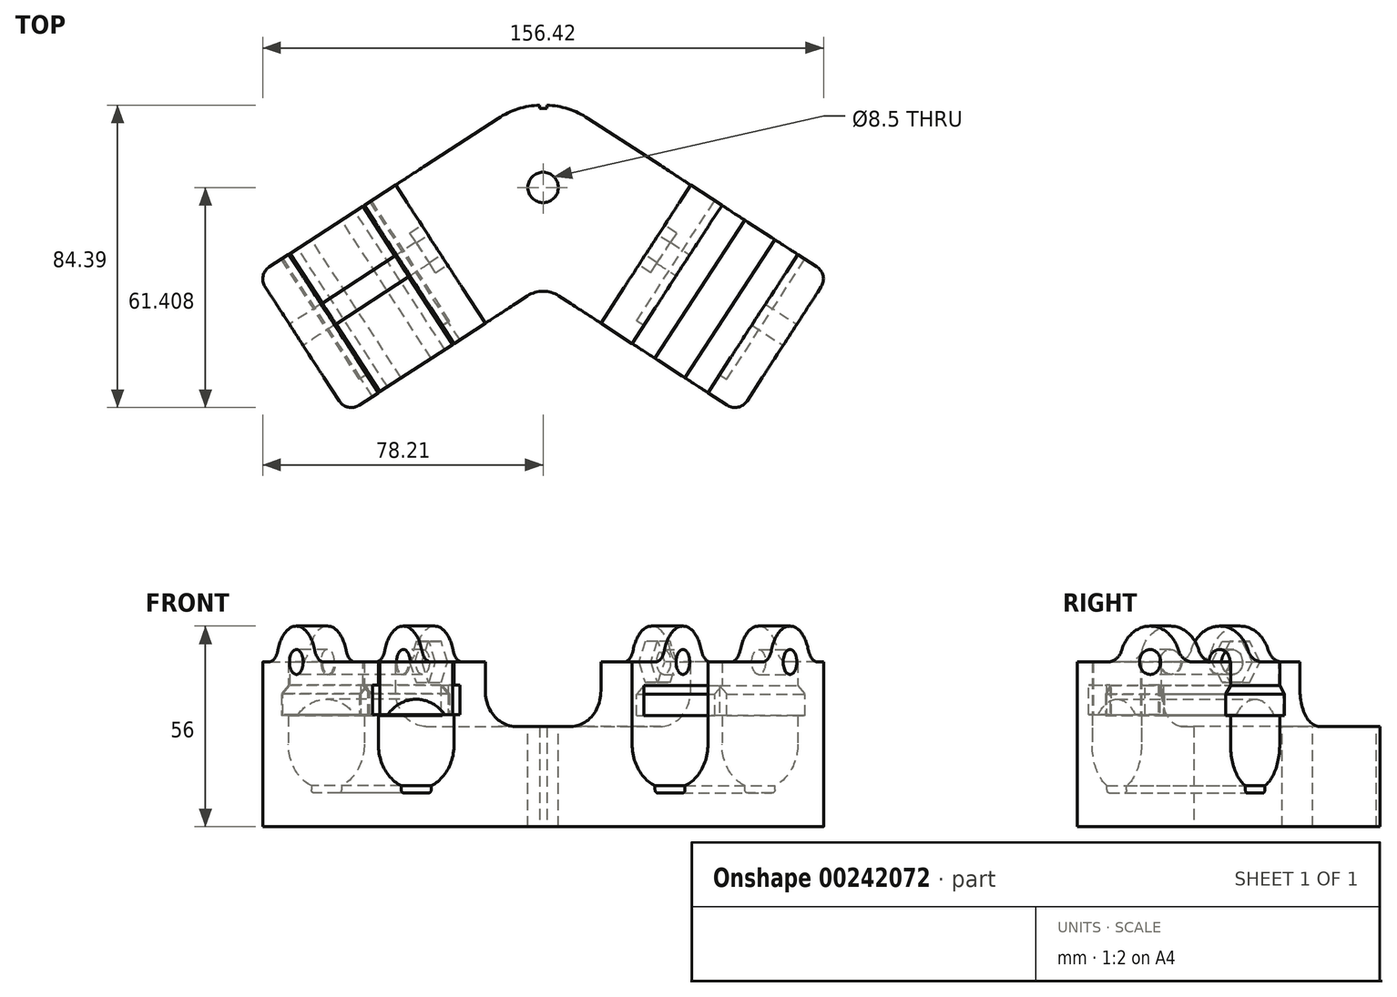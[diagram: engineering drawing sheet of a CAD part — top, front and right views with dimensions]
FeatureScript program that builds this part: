
annotation { "Feature Type Name" : "Feature", "Feature Type Description" : "" }
export const myFeature = defineFeature(function(context is Context, id is Id, definition is map)
    precondition{}
    {
        {
            var Q0;
            Q0=qCreatedBy(makeId("Top.planeOp"),FACE);
            var sketch = newSketch(context, id + "F0", { "sketchPlane" : qUnion([Q0])});
            skCircle(sketch, "E0", {"center": v(0, 0) * mm, "radius": 104.93 * mm, "construction": true});
            skLineSegment(sketch, "E1", {"start": v(0, 0) * mm, "end": v(-57.15, 88) * mm, "construction": true});
            skLineSegment(sketch, "E2", {"start": v(0, 0) * mm, "end": v(57.15, 88) * mm, "construction": true});
            skLineSegment(sketch, "E3", {"start": v(-54.7, 41.99) * mm, "end": v(0, 77.5) * mm});
            skLineSegment(sketch, "E4", {"start": v(-54.7, 41.99) * mm, "end": v(-79.74, 80.57) * mm});
            skLineSegment(sketch, "E5", {"start": v(-79.74, 80.57) * mm, "end": v(-12.53, 124.22) * mm});
            skArc(sketch, "E6", {"start": v(0, 127.93) * mm, "mid": v(-6.53, 126.98) * mm, "end": v(-12.53, 124.22) * mm});
            skLineSegment(sketch, "E7.MirrorCS", {"start": v(54.7, 41.99) * mm, "end": v(0, 77.5) * mm});
            skLineSegment(sketch, "E8.MirrorCS", {"start": v(79.74, 80.57) * mm, "end": v(12.53, 124.22) * mm});
            skLineSegment(sketch, "E9.MirrorCS", {"start": v(54.7, 41.99) * mm, "end": v(79.74, 80.57) * mm});
            skArc(sketch, "E10.MirrorCS", {"start": v(0, 127.93) * mm, "mid": v(6.53, 126.98) * mm, "end": v(12.53, 124.22) * mm});
            skPoint(sketch, "E11", {"position": v(-35.4, 54.51) * mm});
            skPoint(sketch, "E12", {"position": v(35.4, 54.51) * mm});
            skSolve(sketch);
        }
        {
            var Q0;
            Q0=qSketchRegion(id+"F0",true);
            extrude(context, id + "F1", {"entities" : qUnion([Q0]), "endBound" : BoundingType.SYMMETRIC, "depth" : 46 * mm});
        }
        {
            var Q0;
            Q0=qCreatedBy(makeId("Top.planeOp"),FACE);
            var sketch = newSketch(context, id + "F2", { "sketchPlane" : qUnion([Q0])});
            skLineSegment(sketch, "E13", {"start": v(-45.97, 47.65) * mm, "end": v(-71.02, 86.23) * mm});
            skLineSegment(sketch, "E14", {"start": v(-71.02, 86.23) * mm, "end": v(-60.45, 93.1) * mm});
            skLineSegment(sketch, "E15", {"start": v(-60.45, 93.1) * mm, "end": v(-35.4, 54.51) * mm});
            skLineSegment(sketch, "E16", {"start": v(-35.4, 54.51) * mm, "end": v(-45.97, 47.65) * mm});
            skSolve(sketch);
        }
        {
            var Q0;
            Q0=qCreatedBy(makeId("Top.planeOp"),FACE);
            var sketch = newSketch(context, id + "F3", { "sketchPlane" : qUnion([Q0])});
            skLineSegment(sketch, "E17", {"start": v(24.83, 61.38) * mm, "end": v(49.89, 99.95) * mm});
            skLineSegment(sketch, "E18", {"start": v(49.89, 99.95) * mm, "end": v(60.45, 93.1) * mm});
            skLineSegment(sketch, "E19", {"start": v(60.45, 93.1) * mm, "end": v(35.4, 54.51) * mm});
            skLineSegment(sketch, "E20", {"start": v(35.4, 54.51) * mm, "end": v(24.83, 61.38) * mm});
            skSolve(sketch);
        }
        {
            var Q0;
            Q0=qSketchRegion(id+"F2",true);
            var Q1;
            Q1=sQuery(id+"F0.wireOp",EDGE,"E1");
            revolve(context, id + "F4", {"operationType" : NewBodyOperationType.REMOVE, "entities" : qUnion([Q0]), "axis" : qUnion([Q1]), "revolveType" : RevolveType.FULL, "oppositeDirection" : true});
        }
        {
            var Q0;
            Q0=qSketchRegion(id+"F3",true);
            var Q1;
            Q1=sQuery(id+"F0.wireOp",EDGE,"E2");
            revolve(context, id + "F5", {"operationType" : NewBodyOperationType.REMOVE, "entities" : qUnion([Q0]), "axis" : qUnion([Q1]), "revolveType" : RevolveType.FULL, "oppositeDirection" : true});
        }
        {
            var Q0;
            {var subQ0=sQuery(id+"F0.wireOp",EDGE,"E7.MirrorCS");var subQ1=makeQuery(id+"F1.opExtrude","SWEPT_FACE",FACE,{"disambiguationData":[OSD([subQ0])]});var subQ2=sQuery(id+"F0.wireOp",EDGE,"E10.MirrorCS");var subQ3=sQuery(id+"F0.wireOp",EDGE,"E6");var subQ5=sQuery(id+"F0.wireOp",EDGE,"E5");var subQ7=sQuery(id+"F0.wireOp",EDGE,"E3");var subQ8=makeQuery(id+"F1.opExtrude","SWEPT_FACE",FACE,{"disambiguationData":[OSD([subQ7])]});var subQ10=sQuery(id+"F0.wireOp",EDGE,"E8.MirrorCS");var subQ12=sQuery(id+"F0.wireOp",EDGE,"E9.MirrorCS");Q0=makeQuery(id+"F15.boolean.opBoolean","SPLIT",FACE,{"disambiguationData":[TD([subQ8])],"derivedFrom":makeQuery(id+"F14.boolean.opBoolean","SPLIT",FACE,{"disambiguationData":[TD([subQ1])],"derivedFrom":makeQuery(id+"F1.opExtrude","CAP_FACE",FACE,{"disambiguationData":[OSD([subQ7,sQuery(id+"F0.wireOp",EDGE,"E4"),subQ5,subQ3,subQ0,subQ10,subQ12,subQ2])],"isStart":false})})});}
            var sketch = newSketch(context, id + "F6", { "sketchPlane" : qUnion([Q0])});
            skLineSegment(sketch, "E21.0", {"start": v(-41.17, 105.62) * mm, "end": v(-12.53, 124.22) * mm});
            skArc(sketch, "E22.0", {"start": v(0, 127.93) * mm, "mid": v(-6.53, 126.98) * mm, "end": v(-12.53, 124.22) * mm});
            skArc(sketch, "E23.0", {"start": v(0, 127.93) * mm, "mid": v(6.53, 126.98) * mm, "end": v(12.53, 124.22) * mm});
            skLineSegment(sketch, "E24.0", {"start": v(41.17, 105.62) * mm, "end": v(12.53, 124.22) * mm});
            skLineSegment(sketch, "E25.0", {"start": v(16.11, 67.04) * mm, "end": v(0, 77.5) * mm});
            skLineSegment(sketch, "E26.0", {"start": v(-16.11, 67.04) * mm, "end": v(0, 77.5) * mm});
            skLineSegment(sketch, "E27", {"start": v(-41.17, 105.62) * mm, "end": v(-16.11, 67.04) * mm});
            skLineSegment(sketch, "E28", {"start": v(16.11, 67.04) * mm, "end": v(41.17, 105.62) * mm});
            skPoint(sketch, "E29.orphan", {"position": v(-79.74, 80.57) * mm});
            skPoint(sketch, "E30.orphan", {"position": v(-54.7, 41.99) * mm});
            skPoint(sketch, "E31.orphan", {"position": v(54.7, 41.99) * mm});
            skPoint(sketch, "E32.orphan", {"position": v(79.74, 80.57) * mm});
            skSolve(sketch);
        }
        {
            var Q0;
            Q0=qSketchRegion(id+"F6",true);
            extrude(context, id + "F7", {"entities" : qUnion([Q0]), "operationType" : NewBodyOperationType.REMOVE, "oppositeDirection" : true, "depth" : 18 * mm});
        }
        {
            var Q0;
            Q0=makeQuery(id+"F1.opExtrude","SWEPT_FACE",FACE,{"disambiguationData":[OSD([sQuery(id+"F0.wireOp",EDGE,"E4")])]});
            var sketch = newSketch(context, id + "F8", { "sketchPlane" : qUnion([Q0])});
            skCircle(sketch, "E33", {"center": v(-91, 23) * mm, "radius": 10 * mm});
            skSolve(sketch);
        }
        {
            var Q0;
            Q0=makeQuery(id+"F1.opExtrude","SWEPT_FACE",FACE,{"disambiguationData":[OSD([sQuery(id+"F0.wireOp",EDGE,"E9.MirrorCS")])]});
            var sketch = newSketch(context, id + "F9", { "sketchPlane" : qUnion([Q0])});
            skCircle(sketch, "E34", {"center": v(91, 23) * mm, "radius": 10 * mm});
            skSolve(sketch);
        }
        {
            var Q0;
            Q0=qSketchRegion(id+"F8",true);
            var Q1;
            Q1=makeQuery(id+"F7.boolean.opBoolean","COPY",FACE,{"derivedFrom":makeQuery(id+"F7.opExtrude","SWEPT_FACE",FACE,{"disambiguationData":[OSD([sQuery(id+"F6.wireOp",EDGE,"E27")])]})});
            extrude(context, id + "F10", {"entities" : qUnion([Q0]), "operationType" : NewBodyOperationType.ADD, "endBound" : BoundingType.UP_TO_SURFACE, "oppositeDirection" : true, "endBoundEntityFace" : qUnion([Q1]), "depth" : 25 * mm});
        }
        {
            var Q0;
            Q0=qSketchRegion(id+"F9",true);
            var Q1;
            Q1=makeQuery(id+"F7.boolean.opBoolean","COPY",FACE,{"derivedFrom":makeQuery(id+"F7.opExtrude","SWEPT_FACE",FACE,{"disambiguationData":[OSD([sQuery(id+"F6.wireOp",EDGE,"E28")])]})});
            extrude(context, id + "F11", {"entities" : qUnion([Q0]), "operationType" : NewBodyOperationType.ADD, "endBound" : BoundingType.UP_TO_SURFACE, "oppositeDirection" : true, "endBoundEntityFace" : qUnion([Q1]), "depth" : 25 * mm});
        }
        {
            var Q0;
            Q0=qCreatedBy(makeId("Top.planeOp"),FACE);
            var sketch = newSketch(context, id + "F12", { "sketchPlane" : qUnion([Q0])});
            skLineSegment(sketch, "E35.0", {"start": v(-45.97, 47.65) * mm, "end": v(-71.02, 86.23) * mm});
            skLineSegment(sketch, "E36.0", {"start": v(-35.4, 54.51) * mm, "end": v(-45.97, 47.65) * mm});
            skLineSegment(sketch, "E37.0", {"start": v(-71.02, 86.23) * mm, "end": v(-60.45, 93.1) * mm});
            skLineSegment(sketch, "E38.MirrorCS", {"start": v(-35.4, 54.51) * mm, "end": v(-24.83, 61.38) * mm});
            skLineSegment(sketch, "E39.MirrorCS", {"start": v(-24.83, 61.38) * mm, "end": v(-49.89, 99.95) * mm});
            skLineSegment(sketch, "E40.MirrorCS", {"start": v(-49.89, 99.95) * mm, "end": v(-60.45, 93.1) * mm});
            skSolve(sketch);
        }
        {
            var Q0;
            Q0=qCreatedBy(makeId("Top.planeOp"),FACE);
            var sketch = newSketch(context, id + "F13", { "sketchPlane" : qUnion([Q0])});
            skLineSegment(sketch, "E41.0", {"start": v(35.4, 54.51) * mm, "end": v(24.83, 61.38) * mm});
            skLineSegment(sketch, "E42.0", {"start": v(24.83, 61.38) * mm, "end": v(49.89, 99.95) * mm});
            skLineSegment(sketch, "E43.0", {"start": v(49.89, 99.95) * mm, "end": v(60.45, 93.1) * mm});
            skLineSegment(sketch, "E44.MirrorCS", {"start": v(45.97, 47.65) * mm, "end": v(71.02, 86.23) * mm});
            skLineSegment(sketch, "E45.MirrorCS", {"start": v(35.4, 54.51) * mm, "end": v(45.97, 47.65) * mm});
            skLineSegment(sketch, "E46.MirrorCS", {"start": v(71.02, 86.23) * mm, "end": v(60.45, 93.1) * mm});
            skSolve(sketch);
        }
        {
            var Q0;
            Q0=qSketchRegion(id+"F12",true);
            var Q1;
            Q1=makeQuery(id+"F1.opExtrude","CAP_FACE",FACE,{"disambiguationData":[OSD([sQuery(id+"F0.wireOp",EDGE,"E3"),sQuery(id+"F0.wireOp",EDGE,"E4"),sQuery(id+"F0.wireOp",EDGE,"E5"),sQuery(id+"F0.wireOp",EDGE,"E6"),sQuery(id+"F0.wireOp",EDGE,"E7.MirrorCS"),sQuery(id+"F0.wireOp",EDGE,"E8.MirrorCS"),sQuery(id+"F0.wireOp",EDGE,"E9.MirrorCS"),sQuery(id+"F0.wireOp",EDGE,"E10.MirrorCS")])],"isStart":false});
            extrude(context, id + "F14", {"entities" : qUnion([Q0]), "operationType" : NewBodyOperationType.REMOVE, "endBound" : BoundingType.THROUGH_ALL, "endBoundEntityFace" : qUnion([Q1]), "depth" : 25 * mm});
        }
        {
            var Q0;
            Q0=qSketchRegion(id+"F13",true);
            var Q1;
            {var subQ0=sQuery(id+"F0.wireOp",EDGE,"E7.MirrorCS");var subQ1=sQuery(id+"F0.wireOp",EDGE,"E8.MirrorCS");var subQ2=sQuery(id+"F0.wireOp",EDGE,"E9.MirrorCS");Q1=makeQuery(id+"F7.boolean.opBoolean","SPLIT",FACE,{"disambiguationData":[TD([makeQuery(id+"F1.opExtrude","SWEPT_FACE",FACE,{"disambiguationData":[OSD([subQ0])]})])],"derivedFrom":makeQuery(id+"F1.opExtrude","CAP_FACE",FACE,{"disambiguationData":[OSD([sQuery(id+"F0.wireOp",EDGE,"E3"),sQuery(id+"F0.wireOp",EDGE,"E4"),sQuery(id+"F0.wireOp",EDGE,"E5"),sQuery(id+"F0.wireOp",EDGE,"E6"),subQ0,subQ1,subQ2,sQuery(id+"F0.wireOp",EDGE,"E10.MirrorCS")])],"isStart":false})});}
            extrude(context, id + "F15", {"entities" : qUnion([Q0]), "operationType" : NewBodyOperationType.REMOVE, "endBound" : BoundingType.THROUGH_ALL, "endBoundEntityFace" : qUnion([Q1]), "depth" : 25 * mm});
        }
        {
            var Q0;
            Q0=makeQuery(id+"F1.opExtrude","SWEPT_EDGE",EDGE,{"disambiguationData":[OSD([sQuery(id+"F0.wireOp",EDGE,"E3"),sQuery(id+"F0.wireOp",EDGE,"E7.MirrorCS")])]});
            fillet(context, id + "F16", {"entities" : qUnion([Q0]), "radius" : 8 * mm, "tangentPropagation" : true, "allowEdgeOverflow" : false});
        }
        {
            var Q0;
            Q0=makeQuery(id+"F7.boolean.opBoolean","COPY",EDGE,{"derivedFrom":makeQuery(id+"F7.opExtrude","CAP_EDGE",EDGE,{"disambiguationData":[OSD([sQuery(id+"F6.wireOp",EDGE,"E28")])],"isStart":false})});
            var Q1;
            Q1=makeQuery(id+"F7.boolean.opBoolean","COPY",EDGE,{"derivedFrom":makeQuery(id+"F7.opExtrude","CAP_EDGE",EDGE,{"disambiguationData":[OSD([sQuery(id+"F6.wireOp",EDGE,"E27")])],"isStart":false})});
            fillet(context, id + "F17", {"entities" : qUnion([Q0, Q1]), "radius" : 10 * mm, "tangentPropagation" : true, "allowEdgeOverflow" : false});
        }
        {
            var Q0;
            Q0=makeQuery(id+"F1.opExtrude","SWEPT_FACE",FACE,{"disambiguationData":[OSD([sQuery(id+"F0.wireOp",EDGE,"E5")])]});
            var sketch = newSketch(context, id + "F18", { "sketchPlane" : qUnion([Q0])});
            skLineSegment(sketch, "E47.bottom", {"start": v(-12.6, 16.4) * mm, "end": v(12.6, 16.4) * mm});
            skLineSegment(sketch, "E47.top", {"start": v(-15, 8) * mm, "end": v(15, 8) * mm});
            skLineSegment(sketch, "E47.left", {"start": v(-15, 14) * mm, "end": v(-15, 8) * mm});
            skLineSegment(sketch, "E47.right", {"start": v(15, 14) * mm, "end": v(15, 8) * mm});
            skLineSegment(sketch, "E48", {"start": v(-12.6, 16.4) * mm, "end": v(-15, 14) * mm});
            skLineSegment(sketch, "E49", {"start": v(12.6, 16.4) * mm, "end": v(15, 14) * mm});
            skSolve(sketch);
        }
        {
            var Q0;
            Q0=makeQuery(id+"F1.opExtrude","SWEPT_FACE",FACE,{"disambiguationData":[OSD([sQuery(id+"F0.wireOp",EDGE,"E8.MirrorCS")])]});
            var sketch = newSketch(context, id + "F19", { "sketchPlane" : qUnion([Q0])});
            skLineSegment(sketch, "E50.bottom", {"start": v(-15, 8) * mm, "end": v(15, 8) * mm});
            skLineSegment(sketch, "E50.top", {"start": v(-12.6, 16.4) * mm, "end": v(12.6, 16.4) * mm});
            skLineSegment(sketch, "E50.left", {"start": v(-15, 8) * mm, "end": v(-15, 14) * mm});
            skLineSegment(sketch, "E50.right", {"start": v(15, 8) * mm, "end": v(15, 14) * mm});
            skLineSegment(sketch, "E51", {"start": v(-12.6, 16.4) * mm, "end": v(-15, 14) * mm});
            skLineSegment(sketch, "E52", {"start": v(12.6, 16.4) * mm, "end": v(15, 14) * mm});
            skSolve(sketch);
        }
        {
            var Q0;
            Q0=qSketchRegion(id+"F18",true);
            extrude(context, id + "F20", {"entities" : qUnion([Q0]), "operationType" : NewBodyOperationType.REMOVE, "oppositeDirection" : true, "depth" : 40 * mm});
        }
        {
            var Q0;
            Q0=qSketchRegion(id+"F19",true);
            extrude(context, id + "F21", {"entities" : qUnion([Q0]), "operationType" : NewBodyOperationType.REMOVE, "oppositeDirection" : true, "depth" : 40 * mm});
        }
        {
            var Q0;
            Q0=makeQuery(id+"F1.opExtrude","SWEPT_FACE",FACE,{"disambiguationData":[OSD([sQuery(id+"F0.wireOp",EDGE,"E5")])]});
            var sketch = newSketch(context, id + "F22", { "sketchPlane" : qUnion([Q0])});
            skLineSegment(sketch, "E53.bottom", {"start": v(-5, -10.6) * mm, "end": v(5, -10.6) * mm});
            skLineSegment(sketch, "E53.top", {"start": v(-4, -13.6) * mm, "end": v(4, -13.6) * mm});
            skLineSegment(sketch, "E53.left", {"start": v(-5, -10.6) * mm, "end": v(-5, -12.6) * mm});
            skLineSegment(sketch, "E53.right", {"start": v(5, -10.6) * mm, "end": v(5, -12.6) * mm});
            skLineSegment(sketch, "E54", {"start": v(0, 0) * mm, "end": v(0, -16.56) * mm, "construction": true});
            skPoint(sketch, "E54.endSnap0", {"position": v(0, -12.6) * mm});
            skPoint(sketch, "E55", {"position": v(0, -13.6) * mm});
            skPoint(sketch, "E56.visualSharp", {"position": v(-5, -13.6) * mm});
            skArc(sketch, "E56.filletArc", {"start": v(-5, -12.6) * mm, "mid": v(-4.7, -13.3) * mm, "end": v(-4, -13.6) * mm});
            skPoint(sketch, "E57.visualSharp", {"position": v(5, -13.6) * mm});
            skArc(sketch, "E57.filletArc", {"start": v(4, -13.6) * mm, "mid": v(4.7, -13.3) * mm, "end": v(5, -12.6) * mm});
            skSolve(sketch);
        }
        {
            var Q0;
            Q0=makeQuery(id+"F1.opExtrude","SWEPT_FACE",FACE,{"disambiguationData":[OSD([sQuery(id+"F0.wireOp",EDGE,"E8.MirrorCS")])]});
            var sketch = newSketch(context, id + "F23", { "sketchPlane" : qUnion([Q0])});
            skLineSegment(sketch, "E58.bottom", {"start": v(-4, -13.6) * mm, "end": v(4, -13.6) * mm});
            skLineSegment(sketch, "E58.top", {"start": v(-5, -10.6) * mm, "end": v(5, -10.6) * mm});
            skLineSegment(sketch, "E58.left", {"start": v(-5, -12.6) * mm, "end": v(-5, -10.6) * mm});
            skLineSegment(sketch, "E58.right", {"start": v(5, -12.6) * mm, "end": v(5, -10.6) * mm});
            skLineSegment(sketch, "E59", {"start": v(0, 0) * mm, "end": v(0, -15.9) * mm, "construction": true});
            skPoint(sketch, "E59.endSnap0", {"position": v(0, -12.6) * mm});
            skPoint(sketch, "E60", {"position": v(0, -13.6) * mm});
            skPoint(sketch, "E61.visualSharp", {"position": v(-5, -13.6) * mm});
            skArc(sketch, "E61.filletArc", {"start": v(-5, -12.6) * mm, "mid": v(-4.7, -13.3) * mm, "end": v(-4, -13.6) * mm});
            skPoint(sketch, "E62.visualSharp", {"position": v(5, -13.6) * mm});
            skArc(sketch, "E62.filletArc", {"start": v(4, -13.6) * mm, "mid": v(4.7, -13.3) * mm, "end": v(5, -12.6) * mm});
            skSolve(sketch);
        }
        {
            var Q0;
            Q0=qSketchRegion(id+"F22",true);
            var Q1;
            Q1=makeQuery(id+"F1.opExtrude","SWEPT_FACE",FACE,{"disambiguationData":[OSD([sQuery(id+"F0.wireOp",EDGE,"E3")])]});
            extrude(context, id + "F24", {"entities" : qUnion([Q0]), "operationType" : NewBodyOperationType.REMOVE, "endBound" : BoundingType.UP_TO_SURFACE, "oppositeDirection" : true, "endBoundEntityFace" : qUnion([Q1]), "depth" : 25 * mm});
        }
        {
            var Q0;
            Q0=qSketchRegion(id+"F23",true);
            var Q1;
            Q1=makeQuery(id+"F1.opExtrude","SWEPT_FACE",FACE,{"disambiguationData":[OSD([sQuery(id+"F0.wireOp",EDGE,"E7.MirrorCS")])]});
            extrude(context, id + "F25", {"entities" : qUnion([Q0]), "operationType" : NewBodyOperationType.REMOVE, "endBound" : BoundingType.UP_TO_SURFACE, "oppositeDirection" : true, "endBoundEntityFace" : qUnion([Q1]), "depth" : 25 * mm});
        }
        {
            var Q0;
            {var subQ0=sQuery(id+"F9.wireOp",EDGE,"E34");var subQ1=makeQuery(id+"F11.opExtrude","SWEPT_FACE",FACE,{"disambiguationData":[OSD([subQ0])]});var subQ2=sQuery(id+"F0.wireOp",EDGE,"E9.MirrorCS");var subQ3=makeQuery(id+"F1.opExtrude","SWEPT_FACE",FACE,{"disambiguationData":[OSD([subQ2])]});var subQ4=sQuery(id+"F0.wireOp",EDGE,"E8.MirrorCS");var subQ5=sQuery(id+"F0.wireOp",EDGE,"E7.MirrorCS");var subQ6=makeQuery(id+"F1.opExtrude","CAP_FACE",FACE,{"disambiguationData":[OSD([sQuery(id+"F0.wireOp",EDGE,"E3"),sQuery(id+"F0.wireOp",EDGE,"E4"),sQuery(id+"F0.wireOp",EDGE,"E5"),sQuery(id+"F0.wireOp",EDGE,"E6"),subQ5,subQ4,subQ2,sQuery(id+"F0.wireOp",EDGE,"E10.MirrorCS")])],"isStart":false});Q0=makeQuery(id+"F15.boolean.opBoolean","SPLIT",EDGE,{"disambiguationData":[TD([subQ3])],"derivedFrom":makeQuery(id+"F11.boolean.opBoolean","INTERSECT",EDGE,{"disambiguationData":[OD(1.0)],"derivedFrom":[makeQuery(id+"F7.boolean.opBoolean","SPLIT",FACE,{"disambiguationData":[TD([makeQuery(id+"F1.opExtrude","SWEPT_FACE",FACE,{"disambiguationData":[OSD([subQ5])]})])],"derivedFrom":subQ6}),subQ1]})});}
            var Q1;
            {var subQ0=sQuery(id+"F9.wireOp",EDGE,"E34");var subQ1=makeQuery(id+"F11.opExtrude","SWEPT_FACE",FACE,{"disambiguationData":[OSD([subQ0])]});var subQ2=sQuery(id+"F0.wireOp",EDGE,"E9.MirrorCS");var subQ3=makeQuery(id+"F1.opExtrude","SWEPT_FACE",FACE,{"disambiguationData":[OSD([subQ2])]});var subQ4=sQuery(id+"F0.wireOp",EDGE,"E8.MirrorCS");var subQ5=sQuery(id+"F0.wireOp",EDGE,"E7.MirrorCS");var subQ6=makeQuery(id+"F1.opExtrude","CAP_FACE",FACE,{"disambiguationData":[OSD([sQuery(id+"F0.wireOp",EDGE,"E3"),sQuery(id+"F0.wireOp",EDGE,"E4"),sQuery(id+"F0.wireOp",EDGE,"E5"),sQuery(id+"F0.wireOp",EDGE,"E6"),subQ5,subQ4,subQ2,sQuery(id+"F0.wireOp",EDGE,"E10.MirrorCS")])],"isStart":false});Q1=makeQuery(id+"F15.boolean.opBoolean","SPLIT",EDGE,{"disambiguationData":[TD([subQ3])],"derivedFrom":makeQuery(id+"F11.boolean.opBoolean","INTERSECT",EDGE,{"disambiguationData":[OD(0.0)],"derivedFrom":[makeQuery(id+"F7.boolean.opBoolean","SPLIT",FACE,{"disambiguationData":[TD([makeQuery(id+"F1.opExtrude","SWEPT_FACE",FACE,{"disambiguationData":[OSD([subQ5])]})])],"derivedFrom":subQ6}),subQ1]})});}
            var Q2;
            {var subQ0=makeQuery(id+"F11.opExtrude","SWEPT_FACE",FACE,{"disambiguationData":[OSD([sQuery(id+"F9.wireOp",EDGE,"E34")])]});var subQ1=sQuery(id+"F6.wireOp",EDGE,"E28");var subQ2=makeQuery(id+"F7.opExtrude","SWEPT_FACE",FACE,{"disambiguationData":[OSD([subQ1])]});var subQ3=sQuery(id+"F0.wireOp",EDGE,"E9.MirrorCS");var subQ4=sQuery(id+"F0.wireOp",EDGE,"E8.MirrorCS");var subQ5=sQuery(id+"F0.wireOp",EDGE,"E7.MirrorCS");var subQ6=makeQuery(id+"F1.opExtrude","CAP_FACE",FACE,{"disambiguationData":[OSD([sQuery(id+"F0.wireOp",EDGE,"E3"),sQuery(id+"F0.wireOp",EDGE,"E4"),sQuery(id+"F0.wireOp",EDGE,"E5"),sQuery(id+"F0.wireOp",EDGE,"E6"),subQ5,subQ4,subQ3,sQuery(id+"F0.wireOp",EDGE,"E10.MirrorCS")])],"isStart":false});Q2=makeQuery(id+"F15.boolean.opBoolean","SPLIT",EDGE,{"disambiguationData":[TD([makeQuery(id+"F7.boolean.opBoolean","COPY",FACE,{"derivedFrom":subQ2})])],"derivedFrom":makeQuery(id+"F11.boolean.opBoolean","INTERSECT",EDGE,{"disambiguationData":[OD(0.0)],"derivedFrom":[makeQuery(id+"F7.boolean.opBoolean","SPLIT",FACE,{"disambiguationData":[TD([makeQuery(id+"F1.opExtrude","SWEPT_FACE",FACE,{"disambiguationData":[OSD([subQ5])]})])],"derivedFrom":subQ6}),subQ0]})});}
            var Q3;
            {var subQ0=makeQuery(id+"F11.opExtrude","SWEPT_FACE",FACE,{"disambiguationData":[OSD([sQuery(id+"F9.wireOp",EDGE,"E34")])]});var subQ1=sQuery(id+"F6.wireOp",EDGE,"E28");var subQ2=makeQuery(id+"F7.opExtrude","SWEPT_FACE",FACE,{"disambiguationData":[OSD([subQ1])]});var subQ3=sQuery(id+"F0.wireOp",EDGE,"E9.MirrorCS");var subQ4=sQuery(id+"F0.wireOp",EDGE,"E8.MirrorCS");var subQ5=sQuery(id+"F0.wireOp",EDGE,"E7.MirrorCS");var subQ6=makeQuery(id+"F1.opExtrude","CAP_FACE",FACE,{"disambiguationData":[OSD([sQuery(id+"F0.wireOp",EDGE,"E3"),sQuery(id+"F0.wireOp",EDGE,"E4"),sQuery(id+"F0.wireOp",EDGE,"E5"),sQuery(id+"F0.wireOp",EDGE,"E6"),subQ5,subQ4,subQ3,sQuery(id+"F0.wireOp",EDGE,"E10.MirrorCS")])],"isStart":false});Q3=makeQuery(id+"F15.boolean.opBoolean","SPLIT",EDGE,{"disambiguationData":[TD([makeQuery(id+"F7.boolean.opBoolean","COPY",FACE,{"derivedFrom":subQ2})])],"derivedFrom":makeQuery(id+"F11.boolean.opBoolean","INTERSECT",EDGE,{"disambiguationData":[OD(1.0)],"derivedFrom":[makeQuery(id+"F7.boolean.opBoolean","SPLIT",FACE,{"disambiguationData":[TD([makeQuery(id+"F1.opExtrude","SWEPT_FACE",FACE,{"disambiguationData":[OSD([subQ5])]})])],"derivedFrom":subQ6}),subQ0]})});}
            var Q4;
            {var subQ0=makeQuery(id+"F10.opExtrude","SWEPT_FACE",FACE,{"disambiguationData":[OSD([sQuery(id+"F8.wireOp",EDGE,"E33")])]});var subQ1=sQuery(id+"F6.wireOp",EDGE,"E27");var subQ2=makeQuery(id+"F7.opExtrude","SWEPT_FACE",FACE,{"disambiguationData":[OSD([subQ1])]});var subQ3=sQuery(id+"F0.wireOp",EDGE,"E5");var subQ4=sQuery(id+"F0.wireOp",EDGE,"E4");var subQ5=sQuery(id+"F0.wireOp",EDGE,"E3");var subQ6=makeQuery(id+"F1.opExtrude","CAP_FACE",FACE,{"disambiguationData":[OSD([subQ5,subQ4,subQ3,sQuery(id+"F0.wireOp",EDGE,"E6"),sQuery(id+"F0.wireOp",EDGE,"E7.MirrorCS"),sQuery(id+"F0.wireOp",EDGE,"E8.MirrorCS"),sQuery(id+"F0.wireOp",EDGE,"E9.MirrorCS"),sQuery(id+"F0.wireOp",EDGE,"E10.MirrorCS")])],"isStart":false});Q4=makeQuery(id+"F14.boolean.opBoolean","SPLIT",EDGE,{"disambiguationData":[TD([makeQuery(id+"F7.boolean.opBoolean","COPY",FACE,{"derivedFrom":subQ2})])],"derivedFrom":makeQuery(id+"F10.boolean.opBoolean","INTERSECT",EDGE,{"disambiguationData":[OD(1.0)],"derivedFrom":[makeQuery(id+"F7.boolean.opBoolean","SPLIT",FACE,{"disambiguationData":[TD([makeQuery(id+"F1.opExtrude","SWEPT_FACE",FACE,{"disambiguationData":[OSD([subQ5])]})])],"derivedFrom":subQ6}),subQ0]})});}
            var Q5;
            {var subQ0=makeQuery(id+"F10.opExtrude","SWEPT_FACE",FACE,{"disambiguationData":[OSD([sQuery(id+"F8.wireOp",EDGE,"E33")])]});var subQ1=sQuery(id+"F6.wireOp",EDGE,"E27");var subQ2=makeQuery(id+"F7.opExtrude","SWEPT_FACE",FACE,{"disambiguationData":[OSD([subQ1])]});var subQ3=sQuery(id+"F0.wireOp",EDGE,"E5");var subQ4=sQuery(id+"F0.wireOp",EDGE,"E4");var subQ5=sQuery(id+"F0.wireOp",EDGE,"E3");var subQ6=makeQuery(id+"F1.opExtrude","CAP_FACE",FACE,{"disambiguationData":[OSD([subQ5,subQ4,subQ3,sQuery(id+"F0.wireOp",EDGE,"E6"),sQuery(id+"F0.wireOp",EDGE,"E7.MirrorCS"),sQuery(id+"F0.wireOp",EDGE,"E8.MirrorCS"),sQuery(id+"F0.wireOp",EDGE,"E9.MirrorCS"),sQuery(id+"F0.wireOp",EDGE,"E10.MirrorCS")])],"isStart":false});Q5=makeQuery(id+"F14.boolean.opBoolean","SPLIT",EDGE,{"disambiguationData":[TD([makeQuery(id+"F7.boolean.opBoolean","COPY",FACE,{"derivedFrom":subQ2})])],"derivedFrom":makeQuery(id+"F10.boolean.opBoolean","INTERSECT",EDGE,{"disambiguationData":[OD(0.0)],"derivedFrom":[makeQuery(id+"F7.boolean.opBoolean","SPLIT",FACE,{"disambiguationData":[TD([makeQuery(id+"F1.opExtrude","SWEPT_FACE",FACE,{"disambiguationData":[OSD([subQ5])]})])],"derivedFrom":subQ6}),subQ0]})});}
            var Q6;
            {var subQ0=sQuery(id+"F8.wireOp",EDGE,"E33");var subQ1=makeQuery(id+"F10.opExtrude","SWEPT_FACE",FACE,{"disambiguationData":[OSD([subQ0])]});var subQ2=sQuery(id+"F0.wireOp",EDGE,"E4");var subQ3=makeQuery(id+"F1.opExtrude","SWEPT_FACE",FACE,{"disambiguationData":[OSD([subQ2])]});var subQ4=sQuery(id+"F0.wireOp",EDGE,"E5");var subQ5=sQuery(id+"F0.wireOp",EDGE,"E3");var subQ6=makeQuery(id+"F1.opExtrude","CAP_FACE",FACE,{"disambiguationData":[OSD([subQ5,subQ2,subQ4,sQuery(id+"F0.wireOp",EDGE,"E6"),sQuery(id+"F0.wireOp",EDGE,"E7.MirrorCS"),sQuery(id+"F0.wireOp",EDGE,"E8.MirrorCS"),sQuery(id+"F0.wireOp",EDGE,"E9.MirrorCS"),sQuery(id+"F0.wireOp",EDGE,"E10.MirrorCS")])],"isStart":false});Q6=makeQuery(id+"F14.boolean.opBoolean","SPLIT",EDGE,{"disambiguationData":[TD([subQ3])],"derivedFrom":makeQuery(id+"F10.boolean.opBoolean","INTERSECT",EDGE,{"disambiguationData":[OD(0.0)],"derivedFrom":[makeQuery(id+"F7.boolean.opBoolean","SPLIT",FACE,{"disambiguationData":[TD([makeQuery(id+"F1.opExtrude","SWEPT_FACE",FACE,{"disambiguationData":[OSD([subQ5])]})])],"derivedFrom":subQ6}),subQ1]})});}
            var Q7;
            {var subQ0=sQuery(id+"F8.wireOp",EDGE,"E33");var subQ1=makeQuery(id+"F10.opExtrude","SWEPT_FACE",FACE,{"disambiguationData":[OSD([subQ0])]});var subQ2=sQuery(id+"F0.wireOp",EDGE,"E4");var subQ3=makeQuery(id+"F1.opExtrude","SWEPT_FACE",FACE,{"disambiguationData":[OSD([subQ2])]});var subQ4=sQuery(id+"F0.wireOp",EDGE,"E5");var subQ5=sQuery(id+"F0.wireOp",EDGE,"E3");var subQ6=makeQuery(id+"F1.opExtrude","CAP_FACE",FACE,{"disambiguationData":[OSD([subQ5,subQ2,subQ4,sQuery(id+"F0.wireOp",EDGE,"E6"),sQuery(id+"F0.wireOp",EDGE,"E7.MirrorCS"),sQuery(id+"F0.wireOp",EDGE,"E8.MirrorCS"),sQuery(id+"F0.wireOp",EDGE,"E9.MirrorCS"),sQuery(id+"F0.wireOp",EDGE,"E10.MirrorCS")])],"isStart":false});Q7=makeQuery(id+"F14.boolean.opBoolean","SPLIT",EDGE,{"disambiguationData":[TD([subQ3])],"derivedFrom":makeQuery(id+"F10.boolean.opBoolean","INTERSECT",EDGE,{"disambiguationData":[OD(1.0)],"derivedFrom":[makeQuery(id+"F7.boolean.opBoolean","SPLIT",FACE,{"disambiguationData":[TD([makeQuery(id+"F1.opExtrude","SWEPT_FACE",FACE,{"disambiguationData":[OSD([subQ5])]})])],"derivedFrom":subQ6}),subQ1]})});}
            fillet(context, id + "F26", {"entities" : qUnion([Q0, Q1, Q2, Q3, Q4, Q5, Q6, Q7]), "radius" : 5 * mm, "tangentPropagation" : true, "allowEdgeOverflow" : false});
        }
        {
            var Q0;
            Q0=makeQuery(id+"F7.boolean.opBoolean","COPY",FACE,{"derivedFrom":makeQuery(id+"F7.opExtrude","CAP_FACE",FACE,{"disambiguationData":[OSD([sQuery(id+"F6.wireOp",EDGE,"E21.0"),sQuery(id+"F6.wireOp",EDGE,"E22.0"),sQuery(id+"F6.wireOp",EDGE,"E23.0"),sQuery(id+"F6.wireOp",EDGE,"E24.0"),sQuery(id+"F6.wireOp",EDGE,"E25.0"),sQuery(id+"F6.wireOp",EDGE,"E26.0"),sQuery(id+"F6.wireOp",EDGE,"E27"),sQuery(id+"F6.wireOp",EDGE,"E28")])],"isStart":false})});
            var sketch = newSketch(context, id + "F27", { "sketchPlane" : qUnion([Q0])});
            skCircle(sketch, "E63", {"center": v(0, 104.93) * mm, "radius": 4.25 * mm});
            skLineSegment(sketch, "E64", {"start": v(0, 104.93) * mm, "end": v(0, 128.64) * mm, "construction": true});
            skLineSegment(sketch, "E65.bottom", {"start": v(1, 126.93) * mm, "end": v(-1, 126.93) * mm});
            skLineSegment(sketch, "E65.top", {"start": v(1, 128.93) * mm, "end": v(-1, 128.93) * mm});
            skLineSegment(sketch, "E65.left", {"start": v(1, 126.93) * mm, "end": v(1, 128.93) * mm});
            skLineSegment(sketch, "E65.right", {"start": v(-1, 126.93) * mm, "end": v(-1, 128.93) * mm});
            skPoint(sketch, "E66", {"position": v(0, 128.93) * mm});
            skSolve(sketch);
        }
        {
            var Q0;
            Q0=qSketchRegion(id+"F27",true);
            var Q1;
            Q1=makeQuery(id+"F1.opExtrude","CAP_FACE",FACE,{"disambiguationData":[OSD([sQuery(id+"F0.wireOp",EDGE,"E3"),sQuery(id+"F0.wireOp",EDGE,"E4"),sQuery(id+"F0.wireOp",EDGE,"E5"),sQuery(id+"F0.wireOp",EDGE,"E6"),sQuery(id+"F0.wireOp",EDGE,"E7.MirrorCS"),sQuery(id+"F0.wireOp",EDGE,"E8.MirrorCS"),sQuery(id+"F0.wireOp",EDGE,"E9.MirrorCS"),sQuery(id+"F0.wireOp",EDGE,"E10.MirrorCS")])],"isStart":true});
            extrude(context, id + "F28", {"entities" : qUnion([Q0]), "operationType" : NewBodyOperationType.REMOVE, "endBound" : BoundingType.UP_TO_SURFACE, "oppositeDirection" : true, "endBoundEntityFace" : qUnion([Q1]), "depth" : 25 * mm});
        }
        {
            var Q0;
            Q0=makeQuery(id+"F1.opExtrude","SWEPT_FACE",FACE,{"disambiguationData":[OSD([sQuery(id+"F0.wireOp",EDGE,"E5")])]});
            var sketch = newSketch(context, id + "F29", { "sketchPlane" : qUnion([Q0])});
            skArc(sketch, "E67", {"start": v(0, 12.6) * mm, "mid": v(-5.23, 11.46) * mm, "end": v(-9.52, 8.25) * mm});
            skLineSegment(sketch, "E68", {"start": v(-9.52, 8.25) * mm, "end": v(-14.5, 8.25) * mm});
            skLineSegment(sketch, "E69", {"start": v(-14.5, 8.25) * mm, "end": v(-14.5, 14.15) * mm});
            skLineSegment(sketch, "E70", {"start": v(-12.1, 16.55) * mm, "end": v(-12.1, 23) * mm});
            skLineSegment(sketch, "E71", {"start": v(-12.1, 23) * mm, "end": v(0, 23) * mm});
            skLineSegment(sketch, "E72", {"start": v(0, 0) * mm, "end": v(0, 25.7) * mm, "construction": true});
            skLineSegment(sketch, "E73", {"start": v(-14.5, 14.15) * mm, "end": v(-12.1, 16.55) * mm});
            skLineSegment(sketch, "E74.MirrorCS", {"start": v(14.5, 8.25) * mm, "end": v(14.5, 14.15) * mm});
            skLineSegment(sketch, "E75.MirrorCS", {"start": v(12.1, 16.55) * mm, "end": v(12.1, 23) * mm});
            skLineSegment(sketch, "E76.MirrorCS", {"start": v(9.52, 8.25) * mm, "end": v(14.5, 8.25) * mm});
            skArc(sketch, "E77.MirrorCS", {"start": v(0, 12.6) * mm, "mid": v(5.23, 11.46) * mm, "end": v(9.52, 8.25) * mm});
            skLineSegment(sketch, "E78.MirrorCS", {"start": v(14.5, 14.15) * mm, "end": v(12.1, 16.55) * mm});
            skLineSegment(sketch, "E79.MirrorCS", {"start": v(12.1, 23) * mm, "end": v(0, 23) * mm});
            skSolve(sketch);
        }
        {
            var Q0;
            Q0=qSketchRegion(id+"F29",true);
            var Q1;
            Q1=makeQuery(id+"F1.opExtrude","SWEPT_FACE",FACE,{"disambiguationData":[OSD([sQuery(id+"F0.wireOp",EDGE,"E3")])]});
            extrude(context, id + "F30", {"entities" : qUnion([Q0]), "endBound" : BoundingType.UP_TO_SURFACE, "oppositeDirection" : true, "endBoundEntityFace" : qUnion([Q1]), "depth" : 39.5 * mm});
        }
        {
            var Q0;
            Q0=makeQuery(id+"F10.boolean.opBoolean","MERGE",FACE,{"derivedFrom":[makeQuery(id+"F1.opExtrude","SWEPT_FACE",FACE,{"disambiguationData":[OSD([sQuery(id+"F0.wireOp",EDGE,"E4")])]}),makeQuery(id+"F10.opExtrude","CAP_FACE",FACE,{"disambiguationData":[OSD([sQuery(id+"F8.wireOp",EDGE,"E33")])],"isStart":true})]});
            var sketch = newSketch(context, id + "F31", { "sketchPlane" : qUnion([Q0])});
            skCircle(sketch, "E80", {"center": v(-91, 23) * mm, "radius": 3.5 * mm});
            skSolve(sketch);
        }
        {
            var Q0;
            Q0=qSketchRegion(id+"F31",true);
            var Q1;
            {var subQ0=sQuery(id+"F6.wireOp",EDGE,"E27");Q1=makeQuery(id+"F10.boolean.opBoolean","MERGE",FACE,{"derivedFrom":[makeQuery(id+"F7.boolean.opBoolean","COPY",FACE,{"derivedFrom":makeQuery(id+"F7.opExtrude","SWEPT_FACE",FACE,{"disambiguationData":[OSD([subQ0])]})}),makeQuery(id+"F10.opExtrude","CAP_FACE",FACE,{"disambiguationData":[OSD([subQ0])],"isStart":false})]});}
            extrude(context, id + "F32", {"entities" : qUnion([Q0]), "operationType" : NewBodyOperationType.REMOVE, "endBound" : BoundingType.UP_TO_SURFACE, "oppositeDirection" : true, "endBoundEntityFace" : qUnion([Q1]), "depth" : 25 * mm});
        }
        {
            var Q0;
            Q0=makeQuery(id+"F11.boolean.opBoolean","MERGE",FACE,{"derivedFrom":[makeQuery(id+"F1.opExtrude","SWEPT_FACE",FACE,{"disambiguationData":[OSD([sQuery(id+"F0.wireOp",EDGE,"E9.MirrorCS")])]}),makeQuery(id+"F11.opExtrude","CAP_FACE",FACE,{"disambiguationData":[OSD([sQuery(id+"F9.wireOp",EDGE,"E34")])],"isStart":true})]});
            var sketch = newSketch(context, id + "F33", { "sketchPlane" : qUnion([Q0])});
            skCircle(sketch, "E81", {"center": v(91, 23) * mm, "radius": 3.5 * mm});
            skSolve(sketch);
        }
        {
            var Q0;
            Q0=qSketchRegion(id+"F33",true);
            var Q1;
            {var subQ0=sQuery(id+"F6.wireOp",EDGE,"E28");Q1=makeQuery(id+"F11.boolean.opBoolean","MERGE",FACE,{"derivedFrom":[makeQuery(id+"F7.boolean.opBoolean","COPY",FACE,{"derivedFrom":makeQuery(id+"F7.opExtrude","SWEPT_FACE",FACE,{"disambiguationData":[OSD([subQ0])]})}),makeQuery(id+"F11.opExtrude","CAP_FACE",FACE,{"disambiguationData":[OSD([subQ0])],"isStart":false})]});}
            extrude(context, id + "F34", {"entities" : qUnion([Q0]), "operationType" : NewBodyOperationType.REMOVE, "endBound" : BoundingType.UP_TO_SURFACE, "oppositeDirection" : true, "endBoundEntityFace" : qUnion([Q1]), "depth" : 25 * mm});
        }
        {
            var Q0;
            {var subQ0=sQuery(id+"F6.wireOp",EDGE,"E27");Q0=makeQuery(id+"F10.boolean.opBoolean","MERGE",FACE,{"derivedFrom":[makeQuery(id+"F7.boolean.opBoolean","COPY",FACE,{"derivedFrom":makeQuery(id+"F7.opExtrude","SWEPT_FACE",FACE,{"disambiguationData":[OSD([subQ0])]})}),makeQuery(id+"F10.opExtrude","CAP_FACE",FACE,{"disambiguationData":[OSD([subQ0])],"isStart":false})]});}
            var sketch = newSketch(context, id + "F35", { "sketchPlane" : qUnion([Q0])});
            skCircle(sketch, "E82.cCircle", {"center": v(91, 23) * mm, "radius": 5.75 * mm, "construction": true});
            skLineSegment(sketch, "E82.0", {"start": v(84.36, 23) * mm, "end": v(87.68, 28.75) * mm});
            skLineSegment(sketch, "E82.1", {"start": v(87.68, 28.75) * mm, "end": v(94.32, 28.75) * mm});
            skLineSegment(sketch, "E82.2", {"start": v(94.32, 28.75) * mm, "end": v(97.64, 23) * mm});
            skLineSegment(sketch, "E82.3", {"start": v(97.64, 23) * mm, "end": v(94.32, 17.25) * mm});
            skLineSegment(sketch, "E82.4", {"start": v(94.32, 17.25) * mm, "end": v(87.68, 17.25) * mm});
            skLineSegment(sketch, "E82.5", {"start": v(87.68, 17.25) * mm, "end": v(84.36, 23) * mm});
            skPoint(sketch, "E82.0.midPoint", {"position": v(86.02, 25.88) * mm});
            skSolve(sketch);
        }
        {
            var Q0;
            Q0=qSketchRegion(id+"F35",true);
            extrude(context, id + "F36", {"entities" : qUnion([Q0]), "operationType" : NewBodyOperationType.REMOVE, "oppositeDirection" : true, "depth" : 4 * mm});
        }
        {
            var Q0;
            {var subQ0=sQuery(id+"F6.wireOp",EDGE,"E28");Q0=makeQuery(id+"F11.boolean.opBoolean","MERGE",FACE,{"derivedFrom":[makeQuery(id+"F7.boolean.opBoolean","COPY",FACE,{"derivedFrom":makeQuery(id+"F7.opExtrude","SWEPT_FACE",FACE,{"disambiguationData":[OSD([subQ0])]})}),makeQuery(id+"F11.opExtrude","CAP_FACE",FACE,{"disambiguationData":[OSD([subQ0])],"isStart":false})]});}
            var sketch = newSketch(context, id + "F37", { "sketchPlane" : qUnion([Q0])});
            skCircle(sketch, "E83.cCircle", {"center": v(-91, 23) * mm, "radius": 5.75 * mm, "construction": true});
            skLineSegment(sketch, "E83.0", {"start": v(-97.64, 23) * mm, "end": v(-94.32, 28.75) * mm});
            skLineSegment(sketch, "E83.1", {"start": v(-94.32, 28.75) * mm, "end": v(-87.68, 28.75) * mm});
            skLineSegment(sketch, "E83.2", {"start": v(-87.68, 28.75) * mm, "end": v(-84.36, 23) * mm});
            skLineSegment(sketch, "E83.3", {"start": v(-84.36, 23) * mm, "end": v(-87.68, 17.25) * mm});
            skLineSegment(sketch, "E83.4", {"start": v(-87.68, 17.25) * mm, "end": v(-94.32, 17.25) * mm});
            skLineSegment(sketch, "E83.5", {"start": v(-94.32, 17.25) * mm, "end": v(-97.64, 23) * mm});
            skPoint(sketch, "E83.0.midPoint", {"position": v(-95.98, 25.88) * mm});
            skSolve(sketch);
        }
        {
            var Q0;
            Q0=qSketchRegion(id+"F37",true);
            extrude(context, id + "F38", {"entities" : qUnion([Q0]), "operationType" : NewBodyOperationType.REMOVE, "oppositeDirection" : true, "depth" : 4 * mm});
        }
        {
            var Q0;
            Q0=makeQuery(id+"F1.opExtrude","SWEPT_EDGE",EDGE,{"disambiguationData":[OSD([sQuery(id+"F0.wireOp",EDGE,"E8.MirrorCS"),sQuery(id+"F0.wireOp",EDGE,"E9.MirrorCS")])]});
            var Q1;
            Q1=makeQuery(id+"F1.opExtrude","SWEPT_EDGE",EDGE,{"disambiguationData":[OSD([sQuery(id+"F0.wireOp",EDGE,"E7.MirrorCS"),sQuery(id+"F0.wireOp",EDGE,"E9.MirrorCS")])]});
            var Q2;
            Q2=makeQuery(id+"F1.opExtrude","SWEPT_EDGE",EDGE,{"disambiguationData":[OSD([sQuery(id+"F0.wireOp",EDGE,"E3"),sQuery(id+"F0.wireOp",EDGE,"E4")])]});
            var Q3;
            Q3=makeQuery(id+"F1.opExtrude","SWEPT_EDGE",EDGE,{"disambiguationData":[OSD([sQuery(id+"F0.wireOp",EDGE,"E4"),sQuery(id+"F0.wireOp",EDGE,"E5")])]});
            fillet(context, id + "F39", {"entities" : qUnion([Q0, Q1, Q2, Q3]), "radius" : 4 * mm, "tangentPropagation" : true, "allowEdgeOverflow" : false});
        }
        {
            var Q0;
            Q0=makeQuery(id+"F30.opExtrude","SWEPT_FACE",FACE,{"disambiguationData":[OSD([sQuery(id+"F29.wireOp",EDGE,"E74.MirrorCS")])]});
            var sketch = newSketch(context, id + "F40", { "sketchPlane" : qUnion([Q0])});
            skLineSegment(sketch, "E84", {"start": v(-71, 16.55) * mm, "end": v(-71, 8.25) * mm});
            skLineSegment(sketch, "E85", {"start": v(-71, 8.25) * mm, "end": v(-65, 8.25) * mm});
            skLineSegment(sketch, "E86", {"start": v(-65, 8.25) * mm, "end": v(-65, 16.55) * mm});
            skLineSegment(sketch, "E87", {"start": v(-65, 16.55) * mm, "end": v(-71, 16.55) * mm});
            skSolve(sketch);
        }
        {
            var Q0;
            Q0=qSketchRegion(id+"F40",true);
            var Q1;
            Q1=makeQuery(id+"F30.opExtrude","SWEPT_FACE",FACE,{"disambiguationData":[OSD([sQuery(id+"F29.wireOp",EDGE,"E75.MirrorCS")])]});
            extrude(context, id + "F41", {"entities" : qUnion([Q0]), "operationType" : NewBodyOperationType.REMOVE, "endBound" : BoundingType.UP_TO_SURFACE, "oppositeDirection" : true, "endBoundEntityFace" : qUnion([Q1]), "depth" : 25 * mm});
        }
        {
            var Q0;
            Q0=makeQuery(id+"F30.opExtrude","SWEPT_FACE",FACE,{"disambiguationData":[OSD([sQuery(id+"F29.wireOp",EDGE,"E69")])]});
            var sketch = newSketch(context, id + "F42", { "sketchPlane" : qUnion([Q0])});
            skLineSegment(sketch, "E88.0", {"start": v(65, 16.55) * mm, "end": v(71, 16.55) * mm});
            skLineSegment(sketch, "E89.0", {"start": v(71, 16.55) * mm, "end": v(71, 8.25) * mm});
            skLineSegment(sketch, "E90.0", {"start": v(71, 8.25) * mm, "end": v(65, 8.25) * mm});
            skLineSegment(sketch, "E91.0", {"start": v(65, 8.25) * mm, "end": v(65, 16.55) * mm});
            skSolve(sketch);
        }
        {
            var Q0;
            Q0=qSketchRegion(id+"F42",true);
            var Q1;
            Q1=makeQuery(id+"F30.opExtrude","SWEPT_FACE",FACE,{"disambiguationData":[OSD([sQuery(id+"F29.wireOp",EDGE,"E70")])]});
            extrude(context, id + "F43", {"entities" : qUnion([Q0]), "operationType" : NewBodyOperationType.REMOVE, "endBound" : BoundingType.UP_TO_SURFACE, "oppositeDirection" : true, "endBoundEntityFace" : qUnion([Q1]), "depth" : 25 * mm});
        }
    });
